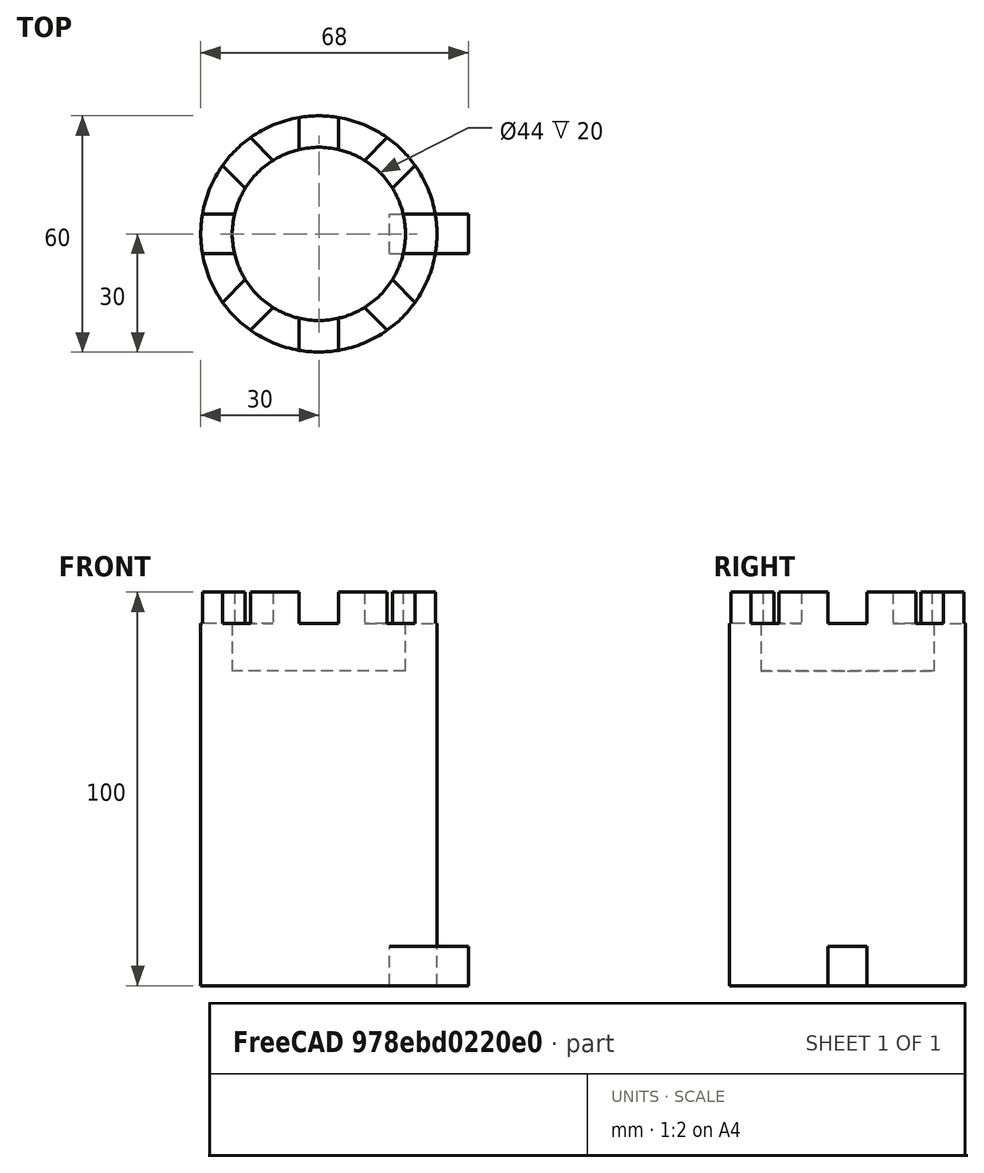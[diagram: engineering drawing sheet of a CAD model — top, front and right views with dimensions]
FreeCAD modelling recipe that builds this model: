
FCSTD DOCUMENT  (FreeCAD 0.21R33694 (Git))
Label: OJT1_T11P03.torre
License: All rights reserved
LicenseURL: http://en.wikipedia.org/wiki/All_rights_reserved
objects: Part::Cylinder×2, Part::Cut×2, Part::Box×1, Part::FeaturePython×1
note: 5 computed .brp shape members not serialized (recipe doc carries the construction recipe); baked Part::Feature solids carry a one-line shape summary decoded from their .brp

FEATURE [Part::Cylinder] Cylinder  label="Cilindre"
  Angle = 360
  AttacherType = Attacher::AttachEngine3D
  FirstAngle = 0
  Height = 100
  Radius = 30
  SecondAngle = 0
FEATURE [Part::Box] Box  label="Cub"
  AttacherType = Attacher::AttachEngine3D
  Height = 10
  Length = 20
  Placement = pos=(18,-5,0) rot=(0,0,1;0rad)
  Width = 10
FEATURE [Part::FeaturePython] Array  # Draft array (typed FeaturePython)
  AlwaysSyncPlacement = false
  Angle = 360
  ArrayType = 1
  Axis = (0,0,1)
  Base = -> Box
  Center = (0,0,0)
  Count = 8
  ExpandArray = false
  Fuse = false
  IntervalAxis = (0,0,0)
  IntervalX = (50,0,0)
  IntervalY = (0,50,0)
  IntervalZ = (0,0,50)
  NumberCircles = 3
  NumberPolar = 8
  NumberX = 2
  NumberY = 2
  NumberZ = 1
  Placement = pos=(0,0,92) rot=(0,0,1;0rad)
  PlacementList = 8 placements: [(18,-5,0),(16.2635,9.19239,0),(5,18,0),(-9.19239,16.2635,0),(-18,5,0),(-16.2635,-9.19239,0),(-5,-18,0),(9.19239,-16.2635,0)]
  RadialDistance = 50
  ScaleList = (8) [(1,1,1),(1,1,1),(1,1,1),(1,1,1),(1,1,1),(1,1,1),(1,1,1),(1,1,1)]
  Symmetry = 1
  TangentialDistance = 25
FEATURE [Part::Cut] Cut
  Base = -> Cylinder
  Refine = true
  Tool = -> Array
FEATURE [Part::Cylinder] Cylinder001  label="Cilindre001"
  Angle = 360
  AttacherType = Attacher::AttachEngine3D
  FirstAngle = 0
  Height = 20
  Placement = pos=(0,0,80) rot=(0,0,1;0rad)
  Radius = 22
  SecondAngle = 0
FEATURE [Part::Cut] Cut001
  Base = -> Cut
  Refine = true
  Tool = -> Cylinder001
